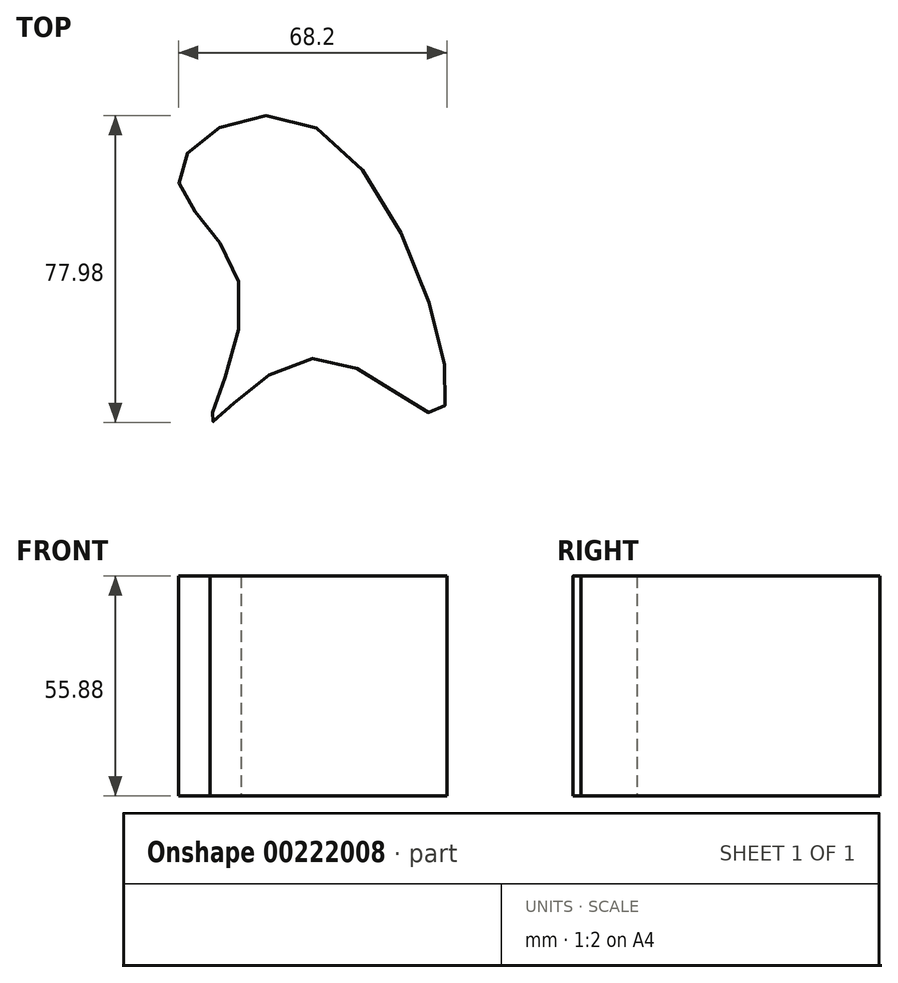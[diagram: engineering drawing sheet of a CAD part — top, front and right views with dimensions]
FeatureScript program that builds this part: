
annotation { "Feature Type Name" : "Feature", "Feature Type Description" : "" }
export const myFeature = defineFeature(function(context is Context, id is Id, definition is map)
    precondition{}
    {
        {
            var Q0;
            Q0=qCreatedBy(makeId("Top.planeOp"),FACE);
            var sketch = newSketch(context, id + "F0", { "sketchPlane" : qUnion([Q0])});
            skFitSpline(sketch, "E0", {"points": [v(0, 40.57) * mm, v(-35.01, 29.09) * mm, v(-19.45, 0) * mm, v(-26.86, -34.27) * mm, v(0, -17.97) * mm, v(31.68, -31.68) * mm, v(0, 40.57) * mm]});
            skSolve(sketch);
        }
        {
            var Q0;
            Q0=makeQuery(id+"F0.imprint","IMPRINT",FACE,{"disambiguationData":[TD([[makeQuery(id+"F0.imprint","IMPRINT",EDGE,{"derivedFrom":sQuery(id+"F0.wireOp",EDGE,"E0")}),1.0]])]});
            extrude(context, id + "F1", {"entities" : qUnion([Q0]), "depth" : 55.88 * mm});
        }
    });
